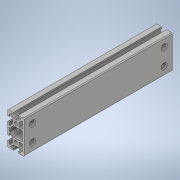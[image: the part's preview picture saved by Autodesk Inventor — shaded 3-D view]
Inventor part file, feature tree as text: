
AUTODESK INVENTOR PART (.ipt)
format: ipt  version: 2022 (Build 260153000, 153)  size: 400,896 bytes
history: native  units: mm
features: other x7, sketch x7, hole x6, extrude x1, pattern_linear x1
ambient origin geometry x8: Origin, YZ Plane, XZ Plane, XY Plane, X Axis, Y Axis, Z Axis, Center Point
bodies: Solid1 (feature_tree)
feature tree (22):
  extrude  "Extrusion1"  Depth=10.0mm TaperAngle=0.0deg
  hole  "Hole1"  [1 undecoded]
  pattern_linear  "Rectangular Pattern1"  Spacing1=10.0mm  [1 undecoded]
  hole  "Hole2"  [1 undecoded]
  hole  "Hole3"  [1 undecoded]
  hole  "Hole6"  [1 undecoded]
  hole  "Hole7"  [1 undecoded]
  other  "C1_XY"
  other  "C1_YZ"
  other  "C1_ZX"
  other  "C1_X"
  other  "C1_Y"
  other  "C1_Z"
  other  "C1_Center"
  hole  "穴12"  [1 undecoded]
  sketch  "Sketch_63"  dims[d50=7.35mm d51=6.0mm d52=4.0mm d53=2.0mm d54=90.0deg d55=20.0mm d56=0.0mm d64=0.0mm d100=10.0mm d101=3.0mm d102=20.0mm d103=10.0mm d104=170.0mm d105=9.0mm d106=6.0mm d107=4.0mm d108=2.0mm d109=90.0deg d110=5.5mm d111=20.594885mm]
  sketch  "Sketch2"  dims[d0=180.0mm d1=0.0mm]
  sketch  "Sketch3"  dims[d2=4.2mm d3=6.0mm d4=4.0mm d5=2.0mm d6=90.0deg d7=180.0mm d8=0.0mm d9=20.0mm d11=20.0mm d12=10.0mm d14=0.0mm]
  sketch  "Sketch4"  dims[d15=7.35mm d16=6.0mm d17=4.0mm d18=2.0mm d19=90.0deg d20=20.0mm d21=0.0mm]
  sketch  "Sketch7"  dims[d22=7.35mm d23=6.0mm d24=4.0mm d25=2.0mm d26=90.0deg d27=20.0mm d28=0.0mm]
  sketch  "Sketch8"  dims[d43=7.35mm d44=6.0mm d45=4.0mm d46=2.0mm d47=90.0deg d48=20.0mm d49=0.0mm]
  sketch  "スケッチ12"
note: 7 required parameter values undecoded (feature->parameter linkage not recoverable at this tier; creation-order binding heuristic only, values carry confidence <= 0.55)
